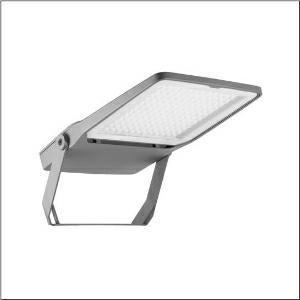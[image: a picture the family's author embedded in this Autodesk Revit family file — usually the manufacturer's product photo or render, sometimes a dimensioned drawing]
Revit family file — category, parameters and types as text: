
# Revit family: floodlight_fl_20_midi___pl61_5xa7682d3c1ac_fcc5
name_source: partatom
category: Lighting Fixtures
units: mm (PartAtom-declared; Revit-internal decimal feet)

## family parameters
Cut with Voids When Loaded = No
Host = Face
Light Source = No
Part Type = Normal
Room Calculation Point = No
Round Connector Dimension = Use Diameter
Shared = No

## types (1)
- --- (1 x LED 5000K / CRI = 70 (unbekannt), 18470 lm, 5000K)
    Apparent Load = 142 VA
    CIE Flux Codes = 33 65 98 100 100
    Color Rendering = 70
    Color Temperature = 5000K
    Default Elevation = 1800 mm
    Description = Floodlight FL 20 midi, floodlight, primary light control with lens, of plastic, primary optical cover: protective disc, of toughened safety glass, transparent, light distribution: PL61, light emission: direct distribution, primary light characteristic: asymmetric, installation type: surface-mounted, LED High Power LED, rated luminous flux: 18.470 lm, light colour: 750, colour temperature: 5000K, control gear: ECG Plus, control: flexible luminous flux parameterisation, time-dependent luminous flux control, digital communication interface, power reduction, overheat protection, electronic power reduction, with terminal, 5-pole, max. 2.5mm², mains connection: 220..240V, AC, 50/60Hz, rated input power: 142W, LED unit, of diecast aluminium, powder-coated, Siteco® metallic grey (DB 702S), length: 654 mm, width: 450 mm, height: 76mm, housing frame, of diecast aluminium, powder-coated, Siteco® metallic grey (DB 702S), mounting bracket, of steel, powder-coated, Siteco® metallic grey (DB 702S), DALIprotection rating (complete): IP66, insulation class (complete): insulation class II (safety insulation), certification: CE, ENEC, VDE, protection symbol: D, permissible ambient temperature for indoor applications: -40..+40°C, permissible ambient temperature for outdoor applications: -40..+50°C, standard: DIN EN 12944, packaging unit: 1 piece

Light Distribution: PL61
    Height = 76 mm
    Lamp = 1 x LED 5000K / CRI >= 70 (unbekannt)
    Lamp Light Flux = 18470 lm
    Lamp count = 1
    Length = 672 mm
    Luminous efficacy = 130 lm/W
    Manufacturer = Siteco
    ModVariant = No
    Model = 5XA7682D3C1AC
    Number of Poles = 1
    OnlyDefault = Yes
    Power Factor = 1
    Product Name = Floodlight FL 20 midi | PL61
    Product group = floodlight | pylon top
    ProductGroupID = 6101
    Protection Class = Protection class II
    Protection Degree = IP 66
    RLX_Detail_Level = 1
    RlxData = <blob elided: 97425 chars, md5=ffa70155>
    Socket = socket
    Standby Power = 0 W
    System Light Flux = 18470 lm
    System Power = 142 W
    Type Comments = factory setting: luminous flux: 100 % | dim-lin: 254 | 489 mA
    Type Image = l_1005943.jpg
    URL = http://relux.com
    VarID = @adj_142535
    Voltage = 0 V
    Weight = 0.00 kg
    Width = 450 mm

## geometry (parser evidence)
native form markers: Blend x4, Sweep x10
no freeform markers — native parametric forms only
